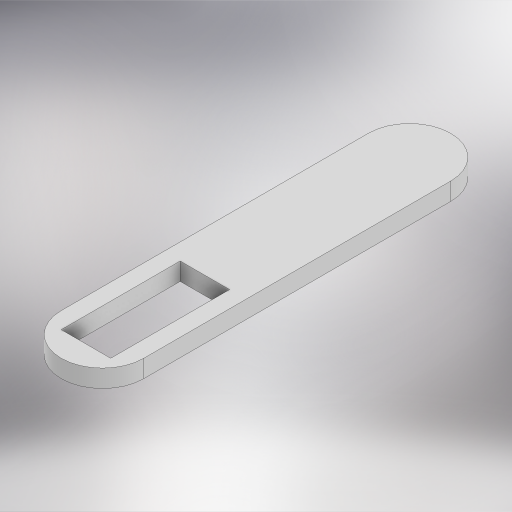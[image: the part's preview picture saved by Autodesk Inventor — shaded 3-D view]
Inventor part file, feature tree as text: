
AUTODESK INVENTOR PART (.ipt)
format: ipt  version: 2024 (Build 280153000, 153)  size: 347,648 bytes
history: native  units: in
note: dims shown in document units (in); Inventor stores cm internally (conversion verified against a paired STEP export)
features: extrude x2, sketch x2, projected_geometry x1
ambient origin geometry x8: Origin, YZ Plane, XZ Plane, XY Plane, X Axis, Y Axis, Z Axis, Center Point
bodies: Solid1 (feature_tree)
feature tree (5):
  extrude  "Extrusion1"  Depth=0.0625in
  extrude  "Extrusion2"  Depth=0.0625in
  sketch  "Sketch1"  dims[d2=0.0625in d3=0.0in d4=0.2165in]
  sketch  "Sketch2"  dims[d5=0.1181in d6=0.1181in d7=0.9449in d8=0.2165in d9=0.0118in d10=0.3346in d11=0.8268in d12=0.1575in d13=1.75in d14=0.125in d15=0.125in d16=0.0079in d17=0.0625in d18=0.0in]
  projected_geometry  "Projected Loop1"
